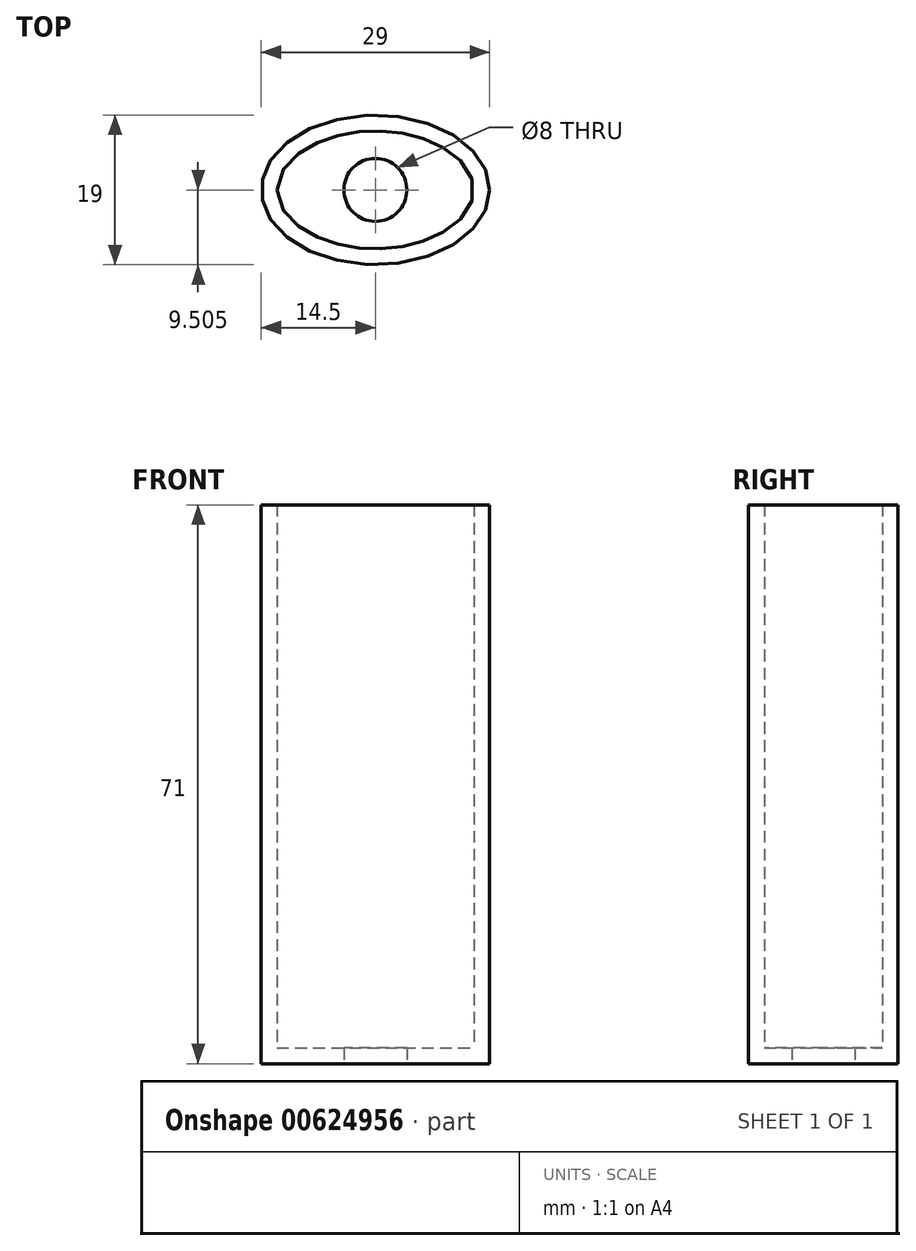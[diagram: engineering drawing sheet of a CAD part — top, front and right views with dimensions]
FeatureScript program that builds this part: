
annotation { "Feature Type Name" : "Feature", "Feature Type Description" : "" }
export const myFeature = defineFeature(function(context is Context, id is Id, definition is map)
    precondition{}
    {
        {
            var Q0;
            Q0=qCreatedBy(makeId("Top.planeOp"),FACE);
            var sketch = newSketch(context, id + "F0", { "sketchPlane" : qUnion([Q0])});
            skEllipse(sketch, "E0", {"center": v(-3.3, -8.74) * mm, "majorRadius": 14.5 * mm, "minorRadius": 9.5 * mm, "majorAxis": v(1, 0)});
            skPoint(sketch, "E1", {"position": v(-17.8, -8.74) * mm});
            skPoint(sketch, "E2", {"position": v(11.2, -8.74) * mm});
            skPoint(sketch, "E3", {"position": v(-3.3, 0.76) * mm});
            skPoint(sketch, "E4", {"position": v(-3.3, -18.24) * mm});
            skSolve(sketch);
        }
        {
            var Q0;
            Q0=qSketchRegion(id+"F0",true);
            extrude(context, id + "F1", {"entities" : qUnion([Q0]), "depth" : 71 * mm, "offsetDistance" : 25 * mm});
        }
        {
            var Q0;
            Q0=makeQuery(id+"F1.opExtrude","CAP_FACE",FACE,{"disambiguationData":[OSD([sQuery(id+"F0.wireOp",EDGE,"E0")])],"isStart":false});
            shell(context, id + "F2", {"entities" : qUnion([Q0]), "thickness" : 2 * mm});
        }
        {
            var Q0;
            Q0=makeQuery(id+"F1.opExtrude","CAP_FACE",FACE,{"disambiguationData":[OSD([sQuery(id+"F0.wireOp",EDGE,"E0")])],"isStart":true});
            var sketch = newSketch(context, id + "F3", { "sketchPlane" : qUnion([Q0])});
            skCircle(sketch, "E5", {"center": v(-3.3, 8.74) * mm, "radius": 4.14 * mm});
            skSolve(sketch);
        }
        {
            var Q0;
            Q0=sQuery(id+"F3.wireOp",VERTEX,"E5.center");
            var Q1;
            Q1=makeQuery(id+"F1.opExtrude","SWEPT_BODY",BODY,{"disambiguationData":[OSD([sQuery(id+"F0.wireOp",EDGE,"E0")])]});
            hole(context, id + "F4", {"style" : HoleStyle.SIMPLE, "endStyle" : HoleEndStyle.THROUGH, "holeDiameter" : 8 * mm, "majorDiameter" : 5 * mm, "isTappedThrough" : true, "tappedDepth" : 12 * mm, "tapClearance" : 3, "locations" : qUnion([Q0]), "scope" : qUnion([Q1])});
        }
    });
